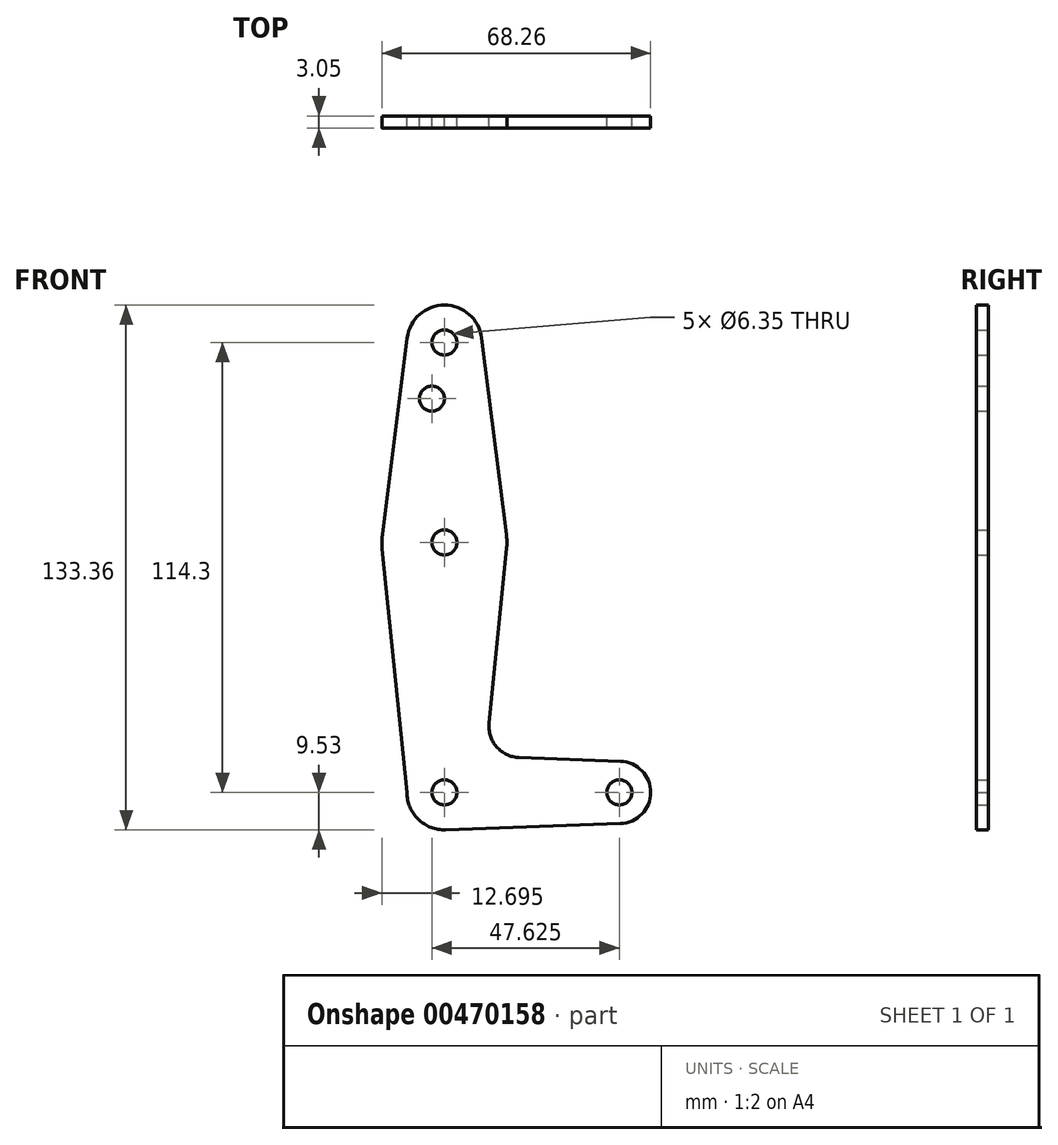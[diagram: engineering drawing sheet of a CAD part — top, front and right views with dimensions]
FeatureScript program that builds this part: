
annotation { "Feature Type Name" : "Feature", "Feature Type Description" : "" }
export const myFeature = defineFeature(function(context is Context, id is Id, definition is map)
    precondition{}
    {
        {
            var Q0;
            Q0=qCreatedBy(makeId("Front.planeOp"),FACE);
            var sketch = newSketch(context, id + "F0", { "sketchPlane" : qUnion([Q0])});
            skLineSegment(sketch, "E0", {"start": v(0, 0) * mm, "end": v(0, 63.5) * mm, "construction": true});
            skCircle(sketch, "E1", {"center": v(0, 63.5) * mm, "radius": 15.88 * mm});
            skLineSegment(sketch, "E2", {"start": v(0, 63.5) * mm, "end": v(0, 114.3) * mm, "construction": true});
            skCircle(sketch, "E3", {"center": v(0, 114.3) * mm, "radius": 9.53 * mm});
            skLineSegment(sketch, "E4", {"start": v(0, 0) * mm, "end": v(44.45, 0) * mm, "construction": true});
            skCircle(sketch, "E5", {"center": v(44.45, 0) * mm, "radius": 7.94 * mm});
            skLineSegment(sketch, "E6", {"start": v(-15.8, 61.9) * mm, "end": v(-9.52, 0) * mm});
            skLineSegment(sketch, "E7", {"start": v(-9.45, 115.5) * mm, "end": v(-15.75, 65.48) * mm});
            skLineSegment(sketch, "E8", {"start": v(9.45, 115.5) * mm, "end": v(15.75, 65.48) * mm});
            skCircle(sketch, "E9", {"center": v(0, 114.3) * mm, "radius": 3.18 * mm});
            skCircle(sketch, "E10", {"center": v(0, 63.5) * mm, "radius": 3.18 * mm});
            skCircle(sketch, "E11", {"center": v(0, 0) * mm, "radius": 3.18 * mm});
            skCircle(sketch, "E12", {"center": v(44.45, 0) * mm, "radius": 3.18 * mm});
            skCircle(sketch, "E13", {"center": v(-3.18, 100.03) * mm, "radius": 3.18 * mm});
            skCircle(sketch, "E14", {"center": v(0, 0) * mm, "radius": 9.53 * mm});
            skLineSegment(sketch, "E15", {"start": v(0.34, -9.52) * mm, "end": v(44.73, -7.93) * mm});
            skLineSegment(sketch, "E16", {"start": v(15.8, 61.91) * mm, "end": v(11.34, 17.6) * mm});
            skLineSegment(sketch, "E17", {"start": v(18.97, 8.85) * mm, "end": v(44.73, 7.93) * mm});
            skArc(sketch, "E18.filletArc", {"start": v(11.34, 17.6) * mm, "mid": v(13.26, 11.57) * mm, "end": v(18.97, 8.85) * mm});
            skSolve(sketch);
        }
        {
            var Q0;
            Q0=makeQuery(id+"F0.imprint","IMPRINT",FACE,{"disambiguationData":[TD([[makeQuery(id+"F0.imprint","IMPRINT",EDGE,{"derivedFrom":sQuery(id+"F0.wireOp",EDGE,"E9")}),-1.0]])]});
            var Q1;
            {var subQ0=sQuery(id+"F0.wireOp",EDGE,"E7");Q1=makeQuery(id+"F0.imprint","IMPRINT",FACE,{"disambiguationData":[TD([[makeQuery(id+"F0.imprint","IMPRINT",EDGE,{"derivedFrom":subQ0}),1.0]])]});}
            var Q2;
            Q2=makeQuery(id+"F0.imprint","IMPRINT",FACE,{"disambiguationData":[TD([[makeQuery(id+"F0.imprint","IMPRINT",EDGE,{"derivedFrom":sQuery(id+"F0.wireOp",EDGE,"E10")}),-1.0]])]});
            var Q3;
            {var subQ0=sQuery(id+"F0.wireOp",EDGE,"E6");Q3=makeQuery(id+"F0.imprint","IMPRINT",FACE,{"disambiguationData":[TD([[makeQuery(id+"F0.imprint","IMPRINT",EDGE,{"derivedFrom":subQ0}),1.0]])]});}
            var Q4;
            Q4=makeQuery(id+"F0.imprint","IMPRINT",FACE,{"disambiguationData":[TD([[makeQuery(id+"F0.imprint","IMPRINT",EDGE,{"derivedFrom":sQuery(id+"F0.wireOp",EDGE,"E11")}),-1.0]])]});
            var Q5;
            Q5=makeQuery(id+"F0.imprint","IMPRINT",FACE,{"disambiguationData":[TD([[makeQuery(id+"F0.imprint","IMPRINT",EDGE,{"derivedFrom":sQuery(id+"F0.wireOp",EDGE,"E12")}),-1.0]])]});
            extrude(context, id + "F1", {"entities" : qUnion([Q0, Q1, Q2, Q3, Q4, Q5]), "depth" : 3.05 * mm});
        }
    });
